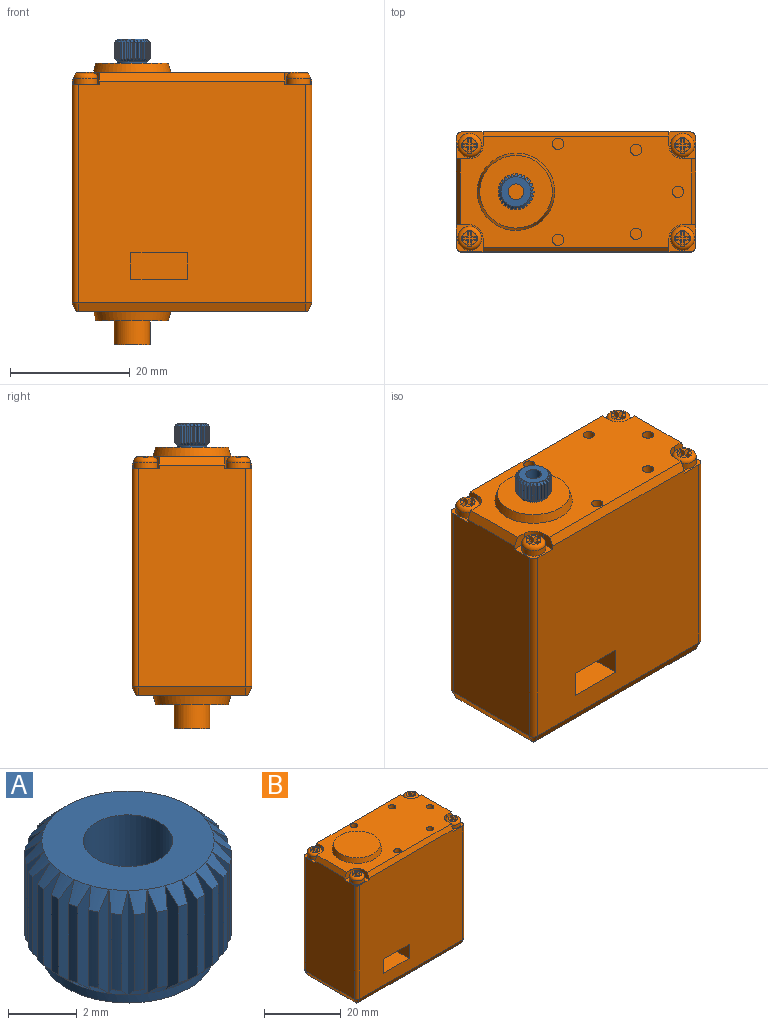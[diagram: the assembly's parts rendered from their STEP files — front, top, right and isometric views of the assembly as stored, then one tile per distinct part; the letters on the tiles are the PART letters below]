
ASSEMBLY  parts=2 mates=1
PART A: 144 faces, bbox 6x6x4 mm
  f0: cone r=3mm half-angle=45deg, axis (0,0,-1), area 0.3mm2, adj f1,f5,f7,f8
  f1: cylinder r=3mm len=2.7mm, axis (0,0,1), area 0.8mm2, adj f0,f2,f7,f8
  f2: cone r=2.5mm half-angle=45deg, axis (0,0,1), area 0.3mm2, adj f1,f6,f7,f8
  f3: plane 5x5mm, normal (0,0,-1), area 14.3mm2, adj f4,f6
  f4: cylinder r=1.3mm len=4mm, axis (0,0,1), area 32.7mm2, adj f3,f5
  f5: plane 5x5mm, normal (0,0,1), area 14.3mm2, adj f0,f4,f9,f14,f19,f24,f29,f34
  f6: cylinder r=2.5mm len=5mm, axis (0,0,1), area 4.7mm2, adj f2,f3,f11,f16,f21,f26,f31,f36
  f7: plane 3.72x0.53mm, normal (-0.23,0.97,0), area 1.7mm2, adj f0,f1,f2,f13
  f8: plane 3.72x0.53mm, normal (-0.23,-0.97,0), area 1.7mm2, adj f0,f1,f2,f142
  f9: cone r=3mm half-angle=45deg, axis (0,0,-1), area 0.3mm2, adj f5,f10,f12,f13
  f10: cylinder r=3mm len=2.7mm, axis (0,0,1), area 0.8mm2, adj f9,f11,f12,f13
  f11: cone r=2.5mm half-angle=45deg, axis (0,0,1), area 0.3mm2, adj f6,f10,f12,f13
  f12: plane 3.72x0.54mm, normal (-0.01,1,0), area 1.7mm2, adj f9,f10,f11,f18
  f13: plane 3.72x0.49mm, normal (-0.45,-0.9,0), area 1.7mm2, adj f7,f9,f10,f11
  f14: cone r=3mm half-angle=45deg, axis (0,0,-1), area 0.3mm2, adj f5,f15,f17,f18
  f15: cylinder r=3mm len=2.7mm, axis (0,0,1), area 0.8mm2, adj f14,f16,f17,f18
  f16: cone r=2.5mm half-angle=45deg, axis (0,0,1), area 0.3mm2, adj f6,f15,f17,f18
  f17: plane 3.72x0.53mm, normal (0.21,0.98,0), area 1.7mm2, adj f14,f15,f16,f23
  f18: plane 3.72x0.42mm, normal (-0.63,-0.77,0), area 1.7mm2, adj f12,f14,f15,f16
  f19: cone r=3mm half-angle=45deg, axis (0,0,-1), area 0.3mm2, adj f5,f20,f22,f23
  f20: cylinder r=3mm len=2.7mm, axis (0,0,1), area 0.8mm2, adj f19,f21,f22,f23
  f21: cone r=2.5mm half-angle=45deg, axis (0,0,1), area 0.3mm2, adj f6,f20,f22,f23
  f22: plane 3.72x0.49mm, normal (0.42,0.91,0), area 1.7mm2, adj f19,f20,f21,f28
  f23: plane 3.72x0.43mm, normal (-0.79,-0.61,0), area 1.7mm2, adj f17,f19,f20,f21
  f24: cone r=3mm half-angle=45deg, axis (0,0,-1), area 0.3mm2, adj f5,f25,f27,f28
  f25: cylinder r=3mm len=2.7mm, axis (0,0,1), area 0.8mm2, adj f24,f26,f27,f28
  f26: cone r=2.5mm half-angle=45deg, axis (0,0,1), area 0.3mm2, adj f6,f25,f27,f28
  f27: plane 3.72x0.43mm, normal (0.61,0.79,0), area 1.7mm2, adj f24,f25,f26,f33
  f28: plane 3.72x0.49mm, normal (-0.91,-0.42,0), area 1.7mm2, adj f22,f24,f25,f26
  f29: cone r=3mm half-angle=45deg, axis (0,0,-1), area 0.3mm2, adj f5,f30,f32,f33
  f30: cylinder r=3mm len=2.7mm, axis (0,0,1), area 0.8mm2, adj f29,f31,f32,f33
  f31: cone r=2.5mm half-angle=45deg, axis (0,0,1), area 0.3mm2, adj f6,f30,f32,f33
  f32: plane 3.72x0.42mm, normal (0.77,0.63,0), area 1.7mm2, adj f29,f30,f31,f38
  f33: plane 3.72x0.53mm, normal (-0.98,-0.21,0), area 1.7mm2, adj f27,f29,f30,f31
  f34: cone r=3mm half-angle=45deg, axis (0,0,-1), area 0.3mm2, adj f5,f35,f37,f38
  f35: cylinder r=3mm len=2.7mm, axis (0,0,1), area 0.8mm2, adj f34,f36,f37,f38
  f36: cone r=2.5mm half-angle=45deg, axis (0,0,1), area 0.3mm2, adj f6,f35,f37,f38
  f37: plane 3.72x0.49mm, normal (0.9,0.45,0), area 1.7mm2, adj f34,f35,f36,f43
  f38: plane 3.72x0.54mm, normal (-1,0.01,0), area 1.7mm2, adj f32,f34,f35,f36
  f39: cone r=3mm half-angle=45deg, axis (0,0,-1), area 0.3mm2, adj f5,f40,f42,f43
  f40: cylinder r=3mm len=2.7mm, axis (0,0,1), area 0.8mm2, adj f39,f41,f42,f43
  f41: cone r=2.5mm half-angle=45deg, axis (0,0,1), area 0.3mm2, adj f6,f40,f42,f43
  f42: plane 3.72x0.53mm, normal (0.97,0.23,0), area 1.7mm2, adj f39,f40,f41,f48
  f43: plane 3.72x0.53mm, normal (-0.97,0.23,0), area 1.7mm2, adj f37,f39,f40,f41
  f44: cone r=3mm half-angle=45deg, axis (0,0,-1), area 0.3mm2, adj f5,f45,f47,f48
  f45: cylinder r=3mm len=2.7mm, axis (0,0,1), area 0.8mm2, adj f44,f46,f47,f48
  f46: cone r=2.5mm half-angle=45deg, axis (0,0,1), area 0.3mm2, adj f6,f45,f47,f48
  f47: plane 3.72x0.54mm, normal (1,0.01,0), area 1.7mm2, adj f44,f45,f46,f53
  f48: plane 3.72x0.49mm, normal (-0.9,0.45,0), area 1.7mm2, adj f42,f44,f45,f46
  f49: cone r=3mm half-angle=45deg, axis (0,0,-1), area 0.3mm2, adj f5,f50,f52,f53
  f50: cylinder r=3mm len=2.7mm, axis (0,0,1), area 0.8mm2, adj f49,f51,f52,f53
  f51: cone r=2.5mm half-angle=45deg, axis (0,0,1), area 0.3mm2, adj f6,f50,f52,f53
  f52: plane 3.72x0.53mm, normal (0.98,-0.21,0), area 1.7mm2, adj f49,f50,f51,f58
  f53: plane 3.72x0.42mm, normal (-0.77,0.63,0), area 1.7mm2, adj f47,f49,f50,f51
  f54: cone r=3mm half-angle=45deg, axis (0,0,-1), area 0.3mm2, adj f5,f55,f57,f58
  f55: cylinder r=3mm len=2.7mm, axis (0,0,1), area 0.8mm2, adj f54,f56,f57,f58
  f56: cone r=2.5mm half-angle=45deg, axis (0,0,1), area 0.3mm2, adj f6,f55,f57,f58
  f57: plane 3.72x0.49mm, normal (0.91,-0.42,0), area 1.7mm2, adj f54,f55,f56,f63
  f58: plane 3.72x0.43mm, normal (-0.61,0.79,0), area 1.7mm2, adj f52,f54,f55,f56
  f59: cone r=3mm half-angle=45deg, axis (0,0,-1), area 0.3mm2, adj f5,f60,f62,f63
  f60: cylinder r=3mm len=2.7mm, axis (0,0,1), area 0.8mm2, adj f59,f61,f62,f63
  f61: cone r=2.5mm half-angle=45deg, axis (0,0,1), area 0.3mm2, adj f6,f60,f62,f63
  f62: plane 3.72x0.43mm, normal (0.79,-0.61,0), area 1.7mm2, adj f59,f60,f61,f68
  f63: plane 3.72x0.49mm, normal (-0.42,0.91,0), area 1.7mm2, adj f57,f59,f60,f61
  f64: cone r=3mm half-angle=45deg, axis (0,0,-1), area 0.3mm2, adj f5,f65,f67,f68
  f65: cylinder r=3mm len=2.7mm, axis (0,0,1), area 0.8mm2, adj f64,f66,f67,f68
  f66: cone r=2.5mm half-angle=45deg, axis (0,0,1), area 0.3mm2, adj f6,f65,f67,f68
  f67: plane 3.72x0.42mm, normal (0.63,-0.77,0), area 1.7mm2, adj f64,f65,f66,f73
  f68: plane 3.72x0.53mm, normal (-0.21,0.98,0), area 1.7mm2, adj f62,f64,f65,f66
  f69: cone r=3mm half-angle=45deg, axis (0,0,-1), area 0.3mm2, adj f5,f70,f72,f73
  f70: cylinder r=3mm len=2.7mm, axis (0,0,1), area 0.8mm2, adj f69,f71,f72,f73
  f71: cone r=2.5mm half-angle=45deg, axis (0,0,1), area 0.3mm2, adj f6,f70,f72,f73
  f72: plane 3.72x0.49mm, normal (0.45,-0.9,0), area 1.7mm2, adj f69,f70,f71,f78
  f73: plane 3.72x0.54mm, normal (0.01,1,0), area 1.7mm2, adj f67,f69,f70,f71
  f74: cone r=3mm half-angle=45deg, axis (0,0,-1), area 0.3mm2, adj f5,f75,f77,f78
  f75: cylinder r=3mm len=2.7mm, axis (0,0,1), area 0.8mm2, adj f74,f76,f77,f78
  f76: cone r=2.5mm half-angle=45deg, axis (0,0,1), area 0.3mm2, adj f6,f75,f77,f78
  f77: plane 3.72x0.53mm, normal (0.23,-0.97,0), area 1.7mm2, adj f74,f75,f76,f83
  f78: plane 3.72x0.53mm, normal (0.23,0.97,0), area 1.7mm2, adj f72,f74,f75,f76
  f79: cone r=3mm half-angle=45deg, axis (0,0,-1), area 0.3mm2, adj f5,f80,f82,f83
  f80: cylinder r=3mm len=2.7mm, axis (0,0,1), area 0.8mm2, adj f79,f81,f82,f83
  f81: cone r=2.5mm half-angle=45deg, axis (0,0,1), area 0.3mm2, adj f6,f80,f82,f83
  f82: plane 3.72x0.54mm, normal (0.01,-1,0), area 1.7mm2, adj f79,f80,f81,f88
  f83: plane 3.72x0.49mm, normal (0.45,0.9,0), area 1.7mm2, adj f77,f79,f80,f81
  f84: cone r=3mm half-angle=45deg, axis (0,0,-1), area 0.3mm2, adj f5,f85,f87,f88
  f85: cylinder r=3mm len=2.7mm, axis (0,0,1), area 0.8mm2, adj f84,f86,f87,f88
  f86: cone r=2.5mm half-angle=45deg, axis (0,0,1), area 0.3mm2, adj f6,f85,f87,f88
  f87: plane 3.72x0.53mm, normal (-0.21,-0.98,0), area 1.7mm2, adj f84,f85,f86,f93
  f88: plane 3.72x0.42mm, normal (0.63,0.77,0), area 1.7mm2, adj f82,f84,f85,f86
  f89: cone r=3mm half-angle=45deg, axis (0,0,-1), area 0.3mm2, adj f5,f90,f92,f93
  f90: cylinder r=3mm len=2.7mm, axis (0,0,1), area 0.8mm2, adj f89,f91,f92,f93
  f91: cone r=2.5mm half-angle=45deg, axis (0,0,1), area 0.3mm2, adj f6,f90,f92,f93
  f92: plane 3.72x0.49mm, normal (-0.42,-0.91,0), area 1.7mm2, adj f89,f90,f91,f98
  f93: plane 3.72x0.43mm, normal (0.79,0.61,0), area 1.7mm2, adj f87,f89,f90,f91
  f94: cone r=3mm half-angle=45deg, axis (0,0,-1), area 0.3mm2, adj f5,f95,f97,f98
  f95: cylinder r=3mm len=2.7mm, axis (0,0,1), area 0.8mm2, adj f94,f96,f97,f98
  f96: cone r=2.5mm half-angle=45deg, axis (0,0,1), area 0.3mm2, adj f6,f95,f97,f98
  f97: plane 3.72x0.43mm, normal (-0.61,-0.79,0), area 1.7mm2, adj f94,f95,f96,f103
  f98: plane 3.72x0.49mm, normal (0.91,0.42,0), area 1.7mm2, adj f92,f94,f95,f96
  f99: cone r=3mm half-angle=45deg, axis (0,0,-1), area 0.3mm2, adj f5,f100,f102,f103
  f100: cylinder r=3mm len=2.7mm, axis (0,0,1), area 0.8mm2, adj f99,f101,f102,f103
  f101: cone r=2.5mm half-angle=45deg, axis (0,0,1), area 0.3mm2, adj f6,f100,f102,f103
  f102: plane 3.72x0.42mm, normal (-0.77,-0.63,0), area 1.7mm2, adj f99,f100,f101,f108
  f103: plane 3.72x0.53mm, normal (0.98,0.21,0), area 1.7mm2, adj f97,f99,f100,f101
  f104: cone r=3mm half-angle=45deg, axis (0,0,-1), area 0.3mm2, adj f5,f105,f107,f108
  f105: cylinder r=3mm len=2.7mm, axis (0,0,1), area 0.8mm2, adj f104,f106,f107,f108
  f106: cone r=2.5mm half-angle=45deg, axis (0,0,1), area 0.3mm2, adj f6,f105,f107,f108
  f107: plane 3.72x0.49mm, normal (-0.9,-0.45,0), area 1.7mm2, adj f104,f105,f106,f113
  f108: plane 3.72x0.54mm, normal (1,-0.01,0), area 1.7mm2, adj f102,f104,f105,f106
  f109: cone r=3mm half-angle=45deg, axis (0,0,-1), area 0.3mm2, adj f5,f110,f112,f113
  f110: cylinder r=3mm len=2.7mm, axis (0,0,1), area 0.8mm2, adj f109,f111,f112,f113
  f111: cone r=2.5mm half-angle=45deg, axis (0,0,1), area 0.3mm2, adj f6,f110,f112,f113
  f112: plane 3.72x0.53mm, normal (-0.97,-0.23,0), area 1.7mm2, adj f109,f110,f111,f118
  f113: plane 3.72x0.53mm, normal (0.97,-0.23,0), area 1.7mm2, adj f107,f109,f110,f111
  f114: cone r=3mm half-angle=45deg, axis (0,0,-1), area 0.3mm2, adj f5,f115,f117,f118
  f115: cylinder r=3mm len=2.7mm, axis (0,0,1), area 0.8mm2, adj f114,f116,f117,f118
  f116: cone r=2.5mm half-angle=45deg, axis (0,0,1), area 0.3mm2, adj f6,f115,f117,f118
  f117: plane 3.72x0.54mm, normal (-1,-0.01,0), area 1.7mm2, adj f114,f115,f116,f123
  f118: plane 3.72x0.49mm, normal (0.9,-0.45,0), area 1.7mm2, adj f112,f114,f115,f116
  f119: cone r=3mm half-angle=45deg, axis (0,0,-1), area 0.3mm2, adj f5,f120,f122,f123
  f120: cylinder r=3mm len=2.7mm, axis (0,0,1), area 0.8mm2, adj f119,f121,f122,f123
  f121: cone r=2.5mm half-angle=45deg, axis (0,0,1), area 0.3mm2, adj f6,f120,f122,f123
  f122: plane 3.72x0.53mm, normal (-0.98,0.21,0), area 1.7mm2, adj f119,f120,f121,f128
  f123: plane 3.72x0.42mm, normal (0.77,-0.63,0), area 1.7mm2, adj f117,f119,f120,f121
  f124: cone r=3mm half-angle=45deg, axis (0,0,-1), area 0.3mm2, adj f5,f125,f127,f128
  f125: cylinder r=3mm len=2.7mm, axis (0,0,1), area 0.8mm2, adj f124,f126,f127,f128
  f126: cone r=2.5mm half-angle=45deg, axis (0,0,1), area 0.3mm2, adj f6,f125,f127,f128
  f127: plane 3.72x0.49mm, normal (-0.91,0.42,0), area 1.7mm2, adj f124,f125,f126,f133
  f128: plane 3.72x0.43mm, normal (0.61,-0.79,0), area 1.7mm2, adj f122,f124,f125,f126
  f129: cone r=3mm half-angle=45deg, axis (0,0,-1), area 0.3mm2, adj f5,f130,f132,f133
  f130: cylinder r=3mm len=2.7mm, axis (0,0,1), area 0.8mm2, adj f129,f131,f132,f133
  f131: cone r=2.5mm half-angle=45deg, axis (0,0,1), area 0.3mm2, adj f6,f130,f132,f133
  f132: plane 3.72x0.43mm, normal (-0.79,0.61,0), area 1.7mm2, adj f129,f130,f131,f138
  f133: plane 3.72x0.49mm, normal (0.42,-0.91,0), area 1.7mm2, adj f127,f129,f130,f131
  f134: cone r=3mm half-angle=45deg, axis (0,0,-1), area 0.3mm2, adj f5,f135,f137,f138
  f135: cylinder r=3mm len=2.7mm, axis (0,0,1), area 0.8mm2, adj f134,f136,f137,f138
  f136: cone r=2.5mm half-angle=45deg, axis (0,0,1), area 0.3mm2, adj f6,f135,f137,f138
  f137: plane 3.72x0.42mm, normal (-0.63,0.77,0), area 1.7mm2, adj f134,f135,f136,f143
  f138: plane 3.72x0.53mm, normal (0.21,-0.98,0), area 1.7mm2, adj f132,f134,f135,f136
  f139: cone r=3mm half-angle=45deg, axis (0,0,-1), area 0.3mm2, adj f5,f140,f142,f143
  f140: cylinder r=3mm len=2.7mm, axis (0,0,1), area 0.8mm2, adj f139,f141,f142,f143
  f141: cone r=2.5mm half-angle=45deg, axis (0,0,1), area 0.3mm2, adj f6,f140,f142,f143
  f142: plane 3.72x0.49mm, normal (-0.45,0.9,0), area 1.7mm2, adj f8,f139,f140,f141
  f143: plane 3.72x0.54mm, normal (-0.01,-1,0), area 1.7mm2, adj f137,f139,f140,f141
PART B: 154 faces, bbox 40x20x47 mm
  f0: plane 38x37mm, normal (0,-1,0), area 1359.1mm2, adj f14,f17,f26,f29,f108,f109,f113,f120
  f1: plane 38x37mm, normal (0,1,0), area 1359mm2, adj f18,f21,f22,f25,f106,f107,f114,f118
  f2: plane 38.6x18.6mm, normal (0,0,1), area 519.7mm2, adj f6,f14,f15,f16,f18,f19,f20,f22
  f3: plane 37x18mm, normal (1,0,0), area 661.8mm2, adj f15,f17,f19,f21,f106,f108,f117,f119
  f4: plane 37x18mm, normal (-1,0,0), area 661.8mm2, adj f23,f25,f27,f29,f107,f109,f110,f121
  f5: plane 38.6x18.6mm, normal (0,0,-1), area 570.2mm2, adj f8,f110,f111,f112,f113,f114,f115,f116
  f6: cone r=6.45mm half-angle=15deg, axis (0,0,-1), area 61mm2, adj f2,f7
  f7: plane 12.1x12.1mm, normal (0,0,1), area 114.9mm2, adj f6
  f8: cone r=6.45mm half-angle=15deg, axis (0,0,1), area 61mm2, adj f5,f9
  f9: plane 12.1x12.1mm, normal (0,0,-1), area 86.6mm2, adj f8,f12
  f10: plane 6x6mm, normal (0,0,-1), area 23mm2, adj f11,f12
  f11: cylinder r=1.3mm len=4mm, axis (0,0,1), area 32.7mm2, adj f10,f13
  f12: cylinder r=3mm len=6mm, axis (0,0,1), area 75.4mm2, adj f9,f10
  f13: plane 2.6x2.6mm, normal (0,0,-1), area 5.3mm2, adj f11
  f14: plane 2.25x2.1mm, normal (1,0,0), area 4.2mm2, adj f0,f2,f16,f17,f120
  f15: plane 2.25x2.1mm, normal (0,-1,0), area 4.2mm2, adj f2,f3,f16,f17,f119
  f16: cylinder r=2.25mm len=2.25mm, axis (0,0,1), area 7.4mm2, adj f2,f14,f15,f17
  f17: plane 4.5x4.5mm, normal (0,0,1), area 6.4mm2, adj f0,f3,f14,f15,f16,f92,f108
  f18: plane 2.25x2.1mm, normal (1,0,0), area 4.2mm2, adj f1,f2,f20,f21,f118
  f19: plane 2.25x2.1mm, normal (0,1,0), area 4.2mm2, adj f2,f3,f20,f21,f119
  f20: cylinder r=2.25mm len=2.25mm, axis (0,0,1), area 7.4mm2, adj f2,f18,f19,f21
  f21: plane 4.5x4.5mm, normal (0,0,1), area 6.4mm2, adj f1,f3,f18,f19,f20,f73,f106
  f22: plane 2.25x2.1mm, normal (-1,0,0), area 4.2mm2, adj f1,f2,f24,f25,f118
  f23: plane 2.25x2.1mm, normal (0,1,0), area 4.2mm2, adj f2,f4,f24,f25,f121
  f24: cylinder r=2.25mm len=2.25mm, axis (0,0,1), area 7.4mm2, adj f2,f22,f23,f25
  f25: plane 4.5x4.5mm, normal (0,0,1), area 6.4mm2, adj f1,f4,f22,f23,f24,f35,f107
  f26: plane 2.25x2.1mm, normal (-1,0,0), area 4.2mm2, adj f0,f2,f28,f29,f120
  f27: plane 2.25x2.1mm, normal (0,-1,0), area 4.2mm2, adj f2,f4,f28,f29,f121
  f28: cylinder r=2.25mm len=2.25mm, axis (0,0,1), area 7.4mm2, adj f2,f26,f27,f29
  f29: plane 4.5x4.5mm, normal (0,0,1), area 6.4mm2, adj f0,f4,f26,f27,f28,f54,f109
  f30: plane 0.78x0.78mm, normal (0,0,1), area 0.4mm2, adj f33,f41,f44
  f31: plane 0.78x0.78mm, normal (0,0,1), area 0.4mm2, adj f33,f37,f45
  f32: plane 0.78x0.78mm, normal (0,0,1), area 0.4mm2, adj f33,f36,f46
  f33: torus R=1.2mm, axis (0,0,1), area 13.1mm2, adj f30,f31,f32,f34,f35,f36,f37,f39
  f34: plane 0.78x0.78mm, normal (0,0,1), area 0.4mm2, adj f33,f39,f47
  f35: cylinder r=2mm len=4mm, axis (0,0,1), area 13.8mm2, adj f25,f33
  f36: plane 1.12x1mm, normal (-0.99,0,0.16), area 1mm2, adj f32,f33,f38,f40,f46
  f37: plane 1.12x1mm, normal (0.99,0,0.16), area 1mm2, adj f31,f33,f38,f40,f45
  f38: plane 2.3x2.3mm, normal (0,0,1), area 1.7mm2, adj f36,f37,f39,f40,f41,f42,f43,f44
  f39: plane 1.12x1mm, normal (-0.99,0,0.16), area 1mm2, adj f33,f34,f38,f42,f47
  f40: plane 0.99x0.73mm, normal (0,0.99,0.16), area 0.6mm2, adj f33,f36,f37,f38
  f41: plane 1.12x1mm, normal (0.99,0,0.16), area 1mm2, adj f30,f33,f38,f42,f44
  f42: plane 0.99x0.73mm, normal (0,-0.99,0.16), area 0.6mm2, adj f33,f38,f39,f41
  f43: plane 0.99x0.73mm, normal (0.99,0,0.16), area 0.6mm2, adj f33,f38,f44,f45
  f44: plane 1.12x1mm, normal (0,-0.99,0.16), area 1mm2, adj f30,f33,f38,f41,f43
  f45: plane 1.12x1mm, normal (0,0.99,0.16), area 1mm2, adj f31,f33,f37,f38,f43
  f46: plane 1.12x1mm, normal (0,0.99,0.16), area 1mm2, adj f32,f33,f36,f38,f48
  f47: plane 1.12x1mm, normal (0,-0.99,0.16), area 1mm2, adj f33,f34,f38,f39,f48
  f48: plane 0.99x0.73mm, normal (-0.99,0,0.16), area 0.6mm2, adj f33,f38,f46,f47
  f49: plane 0.78x0.78mm, normal (0,0,1), area 0.4mm2, adj f52,f60,f63
  f50: plane 0.78x0.78mm, normal (0,0,1), area 0.4mm2, adj f52,f56,f64
  f51: plane 0.78x0.78mm, normal (0,0,1), area 0.4mm2, adj f52,f55,f65
  f52: torus R=1.2mm, axis (0,0,1), area 13.1mm2, adj f49,f50,f51,f53,f54,f55,f56,f58
  f53: plane 0.78x0.78mm, normal (0,0,1), area 0.4mm2, adj f52,f58,f66
  f54: cylinder r=2mm len=4mm, axis (0,0,1), area 13.8mm2, adj f29,f52
  f55: plane 1.12x1mm, normal (-0.99,0,0.16), area 1mm2, adj f51,f52,f57,f59,f65
  f56: plane 1.12x1mm, normal (0.99,0,0.16), area 1mm2, adj f50,f52,f57,f59,f64
  f57: plane 2.3x2.3mm, normal (0,0,1), area 1.7mm2, adj f55,f56,f58,f59,f60,f61,f62,f63
  f58: plane 1.12x1mm, normal (-0.99,0,0.16), area 1mm2, adj f52,f53,f57,f61,f66
  f59: plane 0.99x0.73mm, normal (0,-0.99,0.16), area 0.6mm2, adj f52,f55,f56,f57
  f60: plane 1.12x1mm, normal (0.99,0,0.16), area 1mm2, adj f49,f52,f57,f61,f63
  f61: plane 0.99x0.73mm, normal (0,0.99,0.16), area 0.6mm2, adj f52,f57,f58,f60
  f62: plane 0.99x0.73mm, normal (0.99,0,0.16), area 0.6mm2, adj f52,f57,f63,f64
  f63: plane 1.12x1mm, normal (0,0.99,0.16), area 1mm2, adj f49,f52,f57,f60,f62
  f64: plane 1.12x1mm, normal (0,-0.99,0.16), area 1mm2, adj f50,f52,f56,f57,f62
  f65: plane 1.12x1mm, normal (0,-0.99,0.16), area 1mm2, adj f51,f52,f55,f57,f67
  f66: plane 1.12x1mm, normal (0,0.99,0.16), area 1mm2, adj f52,f53,f57,f58,f67
  f67: plane 0.99x0.73mm, normal (-0.99,0,0.16), area 0.6mm2, adj f52,f57,f65,f66
  f68: plane 0.78x0.78mm, normal (0,0,1), area 0.4mm2, adj f71,f79,f82
  f69: plane 0.78x0.78mm, normal (0,0,1), area 0.4mm2, adj f71,f75,f83
  f70: plane 0.78x0.78mm, normal (0,0,1), area 0.4mm2, adj f71,f74,f84
  f71: torus R=1.2mm, axis (0,0,1), area 13.1mm2, adj f68,f69,f70,f72,f73,f74,f75,f77
  f72: plane 0.78x0.78mm, normal (0,0,1), area 0.4mm2, adj f71,f77,f85
  f73: cylinder r=2mm len=4mm, axis (0,0,1), area 13.8mm2, adj f21,f71
  f74: plane 1.12x1mm, normal (0.99,0,0.16), area 1mm2, adj f70,f71,f76,f78,f84
  f75: plane 1.12x1mm, normal (-0.99,0,0.16), area 1mm2, adj f69,f71,f76,f78,f83
  f76: plane 2.3x2.3mm, normal (0,0,1), area 1.7mm2, adj f74,f75,f77,f78,f79,f80,f81,f82
  f77: plane 1.12x1mm, normal (0.99,0,0.16), area 1mm2, adj f71,f72,f76,f80,f85
  f78: plane 0.99x0.73mm, normal (0,0.99,0.16), area 0.6mm2, adj f71,f74,f75,f76
  f79: plane 1.12x1mm, normal (-0.99,0,0.16), area 1mm2, adj f68,f71,f76,f80,f82
  f80: plane 0.99x0.73mm, normal (0,-0.99,0.16), area 0.6mm2, adj f71,f76,f77,f79
  f81: plane 0.99x0.73mm, normal (-0.99,0,0.16), area 0.6mm2, adj f71,f76,f82,f83
  f82: plane 1.12x1mm, normal (0,-0.99,0.16), area 1mm2, adj f68,f71,f76,f79,f81
  f83: plane 1.12x1mm, normal (0,0.99,0.16), area 1mm2, adj f69,f71,f75,f76,f81
  f84: plane 1.12x1mm, normal (0,0.99,0.16), area 1mm2, adj f70,f71,f74,f76,f86
  f85: plane 1.12x1mm, normal (0,-0.99,0.16), area 1mm2, adj f71,f72,f76,f77,f86
  f86: plane 0.99x0.73mm, normal (0.99,0,0.16), area 0.6mm2, adj f71,f76,f84,f85
  f87: plane 0.78x0.78mm, normal (0,0,1), area 0.4mm2, adj f90,f98,f101
  f88: plane 0.78x0.78mm, normal (0,0,1), area 0.4mm2, adj f90,f94,f102
  f89: plane 0.78x0.78mm, normal (0,0,1), area 0.4mm2, adj f90,f93,f103
  f90: torus R=1.2mm, axis (0,0,1), area 13.1mm2, adj f87,f88,f89,f91,f92,f93,f94,f96
  f91: plane 0.78x0.78mm, normal (0,0,1), area 0.4mm2, adj f90,f96,f104
  f92: cylinder r=2mm len=4mm, axis (0,0,1), area 13.8mm2, adj f17,f90
  f93: plane 1.12x1mm, normal (0.99,0,0.16), area 1mm2, adj f89,f90,f95,f97,f103
  f94: plane 1.12x1mm, normal (-0.99,0,0.16), area 1mm2, adj f88,f90,f95,f97,f102
  f95: plane 2.3x2.3mm, normal (0,0,1), area 1.7mm2, adj f93,f94,f96,f97,f98,f99,f100,f101
  f96: plane 1.12x1mm, normal (0.99,0,0.16), area 1mm2, adj f90,f91,f95,f99,f104
  f97: plane 0.99x0.73mm, normal (0,-0.99,0.16), area 0.6mm2, adj f90,f93,f94,f95
  f98: plane 1.12x1mm, normal (-0.99,0,0.16), area 1mm2, adj f87,f90,f95,f99,f101
  f99: plane 0.99x0.73mm, normal (0,0.99,0.16), area 0.6mm2, adj f90,f95,f96,f98
  f100: plane 0.99x0.73mm, normal (-0.99,0,0.16), area 0.6mm2, adj f90,f95,f101,f102
  f101: plane 1.12x1mm, normal (0,0.99,0.16), area 1mm2, adj f87,f90,f95,f98,f100
  f102: plane 1.12x1mm, normal (0,-0.99,0.16), area 1mm2, adj f88,f90,f94,f95,f100
  f103: plane 1.12x1mm, normal (0,-0.99,0.16), area 1mm2, adj f89,f90,f93,f95,f105
  f104: plane 1.12x1mm, normal (0,0.99,0.16), area 1mm2, adj f90,f91,f95,f96,f105
  f105: plane 0.99x0.73mm, normal (0.99,0,0.16), area 0.6mm2, adj f90,f95,f103,f104
  f106: cylinder r=1mm len=36.4mm, axis (0,0,1), area 57.2mm2, adj f1,f3,f21,f116
  f107: cylinder r=1mm len=36.4mm, axis (0,0,-1), area 57.2mm2, adj f1,f4,f25,f112
  f108: cylinder r=1mm len=36.4mm, axis (0,0,-1), area 57.2mm2, adj f0,f3,f17,f115
  f109: cylinder r=1mm len=36.4mm, axis (0,0,1), area 57.2mm2, adj f0,f4,f29,f111
  f110: plane 18x1.5mm, normal (-0.91,0,-0.42), area 29.8mm2, adj f4,f5,f111,f112
  f111: cone r=0.3mm half-angle=25deg, axis (0,0,1), area 1.7mm2, adj f5,f109,f110,f113
  f112: cone r=0.3mm half-angle=25deg, axis (0,0,1), area 1.7mm2, adj f5,f107,f110,f114
  f113: plane 38x1.5mm, normal (0,-0.91,-0.42), area 62.9mm2, adj f0,f5,f111,f115
  f114: plane 38x1.5mm, normal (0,0.91,-0.42), area 62.9mm2, adj f1,f5,f112,f116
  f115: cone r=0.3mm half-angle=25deg, axis (0,0,1), area 1.7mm2, adj f5,f108,f113,f117
  f116: cone r=0.3mm half-angle=25deg, axis (0,0,1), area 1.7mm2, adj f5,f106,f114,f117
  f117: plane 18x1.5mm, normal (0.91,0,-0.42), area 29.8mm2, adj f3,f5,f115,f116
  f118: plane 31x1.5mm, normal (0,0.91,0.42), area 51.3mm2, adj f1,f2,f18,f22
  f119: plane 11x1.5mm, normal (0.91,0,0.42), area 18.2mm2, adj f2,f3,f15,f19
  f120: plane 31x1.5mm, normal (0,-0.91,0.42), area 51.3mm2, adj f0,f2,f14,f26
  f121: plane 11x1.5mm, normal (-0.91,0,0.42), area 18.2mm2, adj f2,f4,f23,f27
  f122: cylinder r=0.95mm len=9mm, axis (0,0,1), area 53.7mm2, adj f2,f123
  f123: plane 1.9x1.9mm, normal (0,0,1), area 2.8mm2, adj f122
  f124: cylinder r=0.95mm len=9mm, axis (0,0,1), area 53.7mm2, adj f2,f125
  f125: plane 1.9x1.9mm, normal (0,0,1), area 2.8mm2, adj f124
  f126: cylinder r=0.95mm len=9mm, axis (0,0,1), area 53.7mm2, adj f2,f127
  f127: plane 1.9x1.9mm, normal (0,0,1), area 2.8mm2, adj f126
  f128: cylinder r=0.95mm len=9mm, axis (0,0,1), area 53.7mm2, adj f2,f129
  f129: plane 1.9x1.9mm, normal (0,0,1), area 2.8mm2, adj f128
  f130: cylinder r=0.95mm len=9mm, axis (0,0,1), area 53.7mm2, adj f2,f131
  f131: plane 1.9x1.9mm, normal (0,0,1), area 2.8mm2, adj f130
  f132: cylinder r=0.95mm len=9mm, axis (0,0,-1), area 53.7mm2, adj f5,f133
  f133: plane 1.9x1.9mm, normal (0,0,-1), area 2.8mm2, adj f132
  f134: cylinder r=0.95mm len=9mm, axis (0,0,-1), area 53.7mm2, adj f5,f135
  f135: plane 1.9x1.9mm, normal (0,0,-1), area 2.8mm2, adj f134
  f136: cylinder r=0.95mm len=9mm, axis (0,0,-1), area 53.7mm2, adj f5,f137
  f137: plane 1.9x1.9mm, normal (0,0,-1), area 2.8mm2, adj f136
  f138: cylinder r=0.95mm len=9mm, axis (0,0,-1), area 53.7mm2, adj f5,f139
  f139: plane 1.9x1.9mm, normal (0,0,-1), area 2.8mm2, adj f138
  f140: cylinder r=0.95mm len=9mm, axis (0,0,-1), area 53.7mm2, adj f5,f141
  f141: plane 1.9x1.9mm, normal (0,0,-1), area 2.8mm2, adj f140
  f142: cylinder r=0.95mm len=9mm, axis (0,0,-1), area 53.7mm2, adj f5,f143
  f143: plane 1.9x1.9mm, normal (0,0,-1), area 2.8mm2, adj f142
  f144: plane 9.5x8mm, normal (0,0,-1), area 76mm2, adj f1,f145,f147,f148
  f145: plane 8x4.5mm, normal (1,0,0), area 36mm2, adj f1,f144,f146,f148
  f146: plane 9.5x8mm, normal (0,0,1), area 76mm2, adj f1,f145,f147,f148
  f147: plane 8x4.5mm, normal (-1,0,0), area 36mm2, adj f1,f144,f146,f148
  f148: plane 9.5x4.5mm, normal (0,1,0), area 42.8mm2, adj f144,f145,f146,f147
  f149: plane 9.5x8mm, normal (0,0,-1), area 76mm2, adj f0,f150,f152,f153
  f150: plane 8x4.5mm, normal (1,0,0), area 36mm2, adj f0,f149,f151,f153
  f151: plane 9.5x8mm, normal (0,0,1), area 76mm2, adj f0,f150,f152,f153
  f152: plane 8x4.5mm, normal (-1,0,0), area 36mm2, adj f0,f149,f151,f153
  f153: plane 9.5x4.5mm, normal (0,-1,0), area 42.8mm2, adj f149,f150,f151,f152
PLACE A rot(axis=(0,0,-1),26.5deg) t=(8.95,-4.47,0.12)mm
PLACE B t=(10,0,0.12)mm
MATE revolute A.f0 <-> B.f6  axis (0,0,-1) through (0,0,21.62)mm
